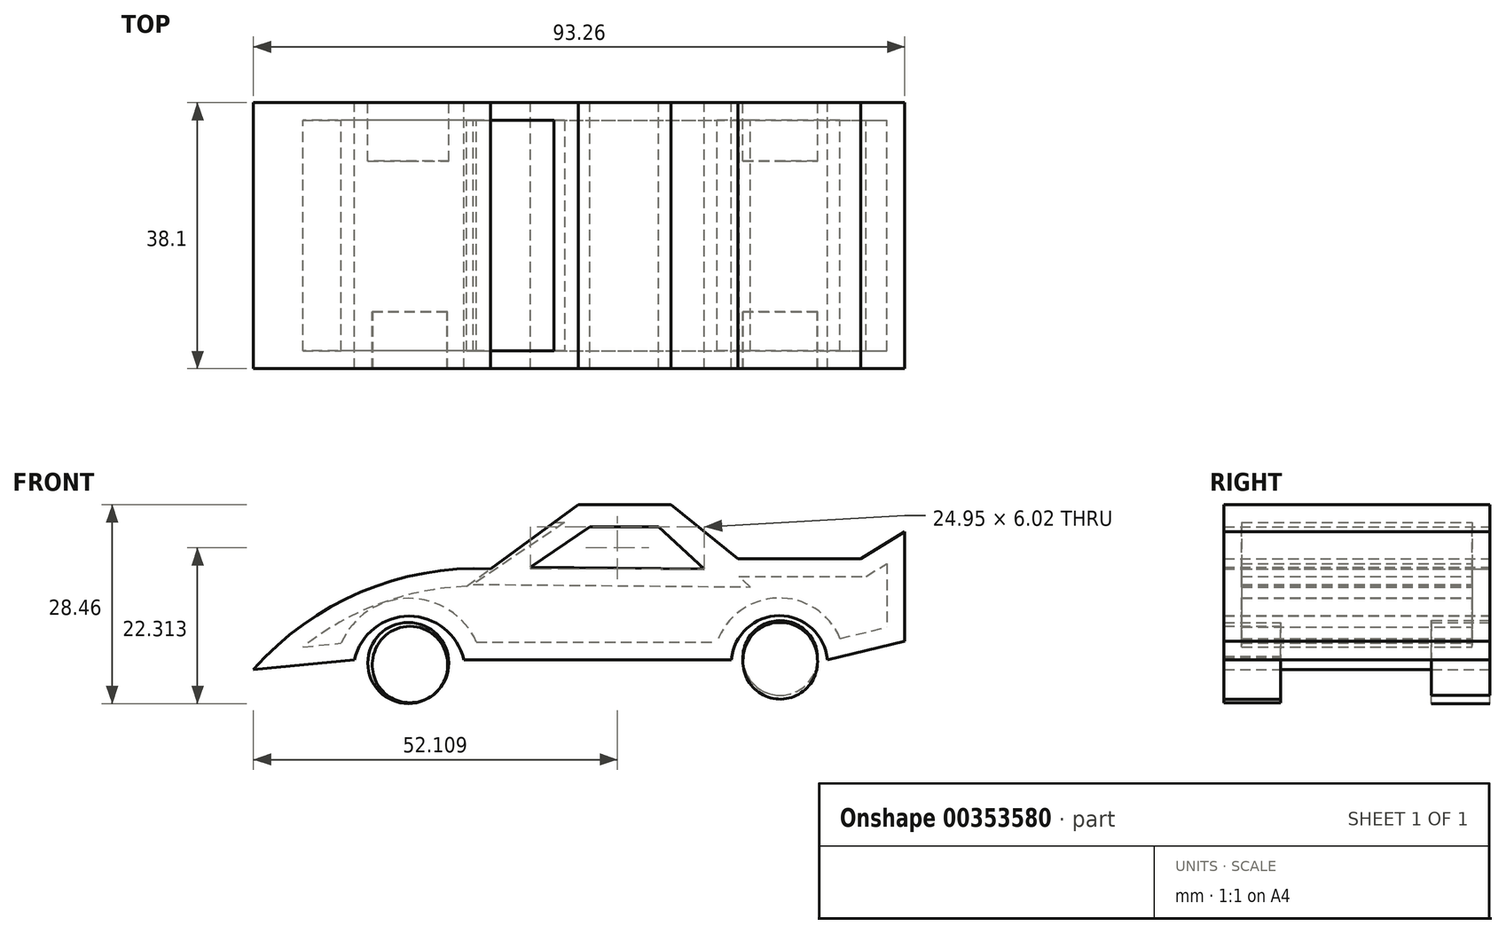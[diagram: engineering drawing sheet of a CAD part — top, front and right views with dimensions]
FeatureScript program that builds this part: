
annotation { "Feature Type Name" : "Feature", "Feature Type Description" : "" }
export const myFeature = defineFeature(function(context is Context, id is Id, definition is map)
    precondition{}
    {
        {
            var Q0;
            Q0=qCreatedBy(makeId("Front.planeOp"),FACE);
            var sketch = newSketch(context, id + "F0", { "sketchPlane" : qUnion([Q0])});
            skArc(sketch, "E0", {"start": v(-11.45, -32.17) * mm, "mid": v(-19.28, -25.94) * mm, "end": v(-27.11, -32.17) * mm});
            skLineSegment(sketch, "E1", {"start": v(-11.45, -32.17) * mm, "end": v(26.87, -32.17) * mm});
            skArc(sketch, "E2", {"start": v(40.6, -32.17) * mm, "mid": v(33.74, -25.88) * mm, "end": v(26.87, -32.17) * mm});
            skLineSegment(sketch, "E3", {"start": v(40.6, -32.17) * mm, "end": v(51.7, -29.52) * mm});
            skLineSegment(sketch, "E4", {"start": v(4.94, -10) * mm, "end": v(18.2, -10) * mm});
            skLineSegment(sketch, "E5", {"start": v(18.2, -10) * mm, "end": v(27.83, -17.71) * mm});
            skLineSegment(sketch, "E6", {"start": v(27.83, -17.71) * mm, "end": v(45.43, -17.71) * mm});
            skLineSegment(sketch, "E7", {"start": v(45.43, -17.71) * mm, "end": v(51.7, -13.86) * mm});
            skLineSegment(sketch, "E8", {"start": v(51.7, -13.86) * mm, "end": v(51.7, -29.52) * mm});
            skLineSegment(sketch, "E9", {"start": v(-7.6, -19.16) * mm, "end": v(4.94, -10) * mm});
            skLineSegment(sketch, "E10", {"start": v(6.63, -13.13) * mm, "end": v(-2.29, -19.16) * mm});
            skLineSegment(sketch, "E11", {"start": v(-2.29, -18.92) * mm, "end": v(23.01, -19.16) * mm});
            skLineSegment(sketch, "E12", {"start": v(6.63, -13.13) * mm, "end": v(16.45, -13.13) * mm});
            skLineSegment(sketch, "E13", {"start": v(23.01, -19.16) * mm, "end": v(16.45, -13.13) * mm});
            skArc(sketch, "E14", {"start": v(-7.6, -19.16) * mm, "mid": v(-26.23, -22.5) * mm, "end": v(-41.57, -33.62) * mm});
            skLineSegment(sketch, "E15", {"start": v(-41.57, -33.62) * mm, "end": v(-27.11, -32.17) * mm});
            skSolve(sketch);
        }
        {
            var Q0;
            Q0 = qSketchRegion(id + "F0", true);
            extrude(context, id + "F1", {"entities" : qUnion([Q0]), "depth" : 38.1 * mm, "offsetDistance" : 25.4 * mm});
        }
        {
            var Q0;
            Q0=makeQuery(id+"F1.opExtrude","SWEPT_FACE",FACE,{"disambiguationData":[OSD([sQuery(id+"F0.wireOp",EDGE,"E9")])]});
            shell(context, id + "F2", {"entities" : qUnion([Q0]), "thickness" : 2.54 * mm});
        }
        {
            var Q0;
            Q0=qCreatedBy(makeId("Front.planeOp"),FACE);
            var sketch = newSketch(context, id + "F3", { "sketchPlane" : qUnion([Q0])});
            skArc(sketch, "E16", {"start": v(39.16, -31.7) * mm, "mid": v(33.75, -26.84) * mm, "end": v(28.56, -31.93) * mm});
            skArc(sketch, "E17", {"start": v(28.56, -31.93) * mm, "mid": v(34, -37.82) * mm, "end": v(39.16, -31.7) * mm});
            skArc(sketch, "E18", {"start": v(-13.86, -31.93) * mm, "mid": v(-19.16, -27.4) * mm, "end": v(-24.46, -31.93) * mm});
            skArc(sketch, "E19", {"start": v(-24.46, -31.93) * mm, "mid": v(-19.16, -38.34) * mm, "end": v(-13.86, -31.93) * mm});
            skSolve(sketch);
        }
        {
            var Q0;
            Q0 = qSketchRegion(id + "F3", true);
            extrude(context, id + "F4", {"entities" : qUnion([Q0]), "depth" : 38.1 * mm, "offsetDistance" : 25.4 * mm, "hasSecondDirection" : true, "secondDirectionOppositeDirection" : false, "secondDirectionDepth" : 29.97 * mm});
        }
        {
            var Q0;
            Q0=qCreatedBy(makeId("Front.planeOp"),FACE);
            var sketch = newSketch(context, id + "F5", { "sketchPlane" : qUnion([Q0])});
            skCircle(sketch, "E20", {"center": v(33.86, -31.93) * mm, "radius": 5.35 * mm});
            skCircle(sketch, "E21", {"center": v(-19.4, -32.65) * mm, "radius": 5.8 * mm});
            skSolve(sketch);
        }
        {
            var Q0;
            Q0 = qSketchRegion(id + "F5", true);
            extrude(context, id + "F6", {"entities" : qUnion([Q0]), "depth" : 8.38 * mm, "offsetDistance" : 25.4 * mm});
        }
    });
